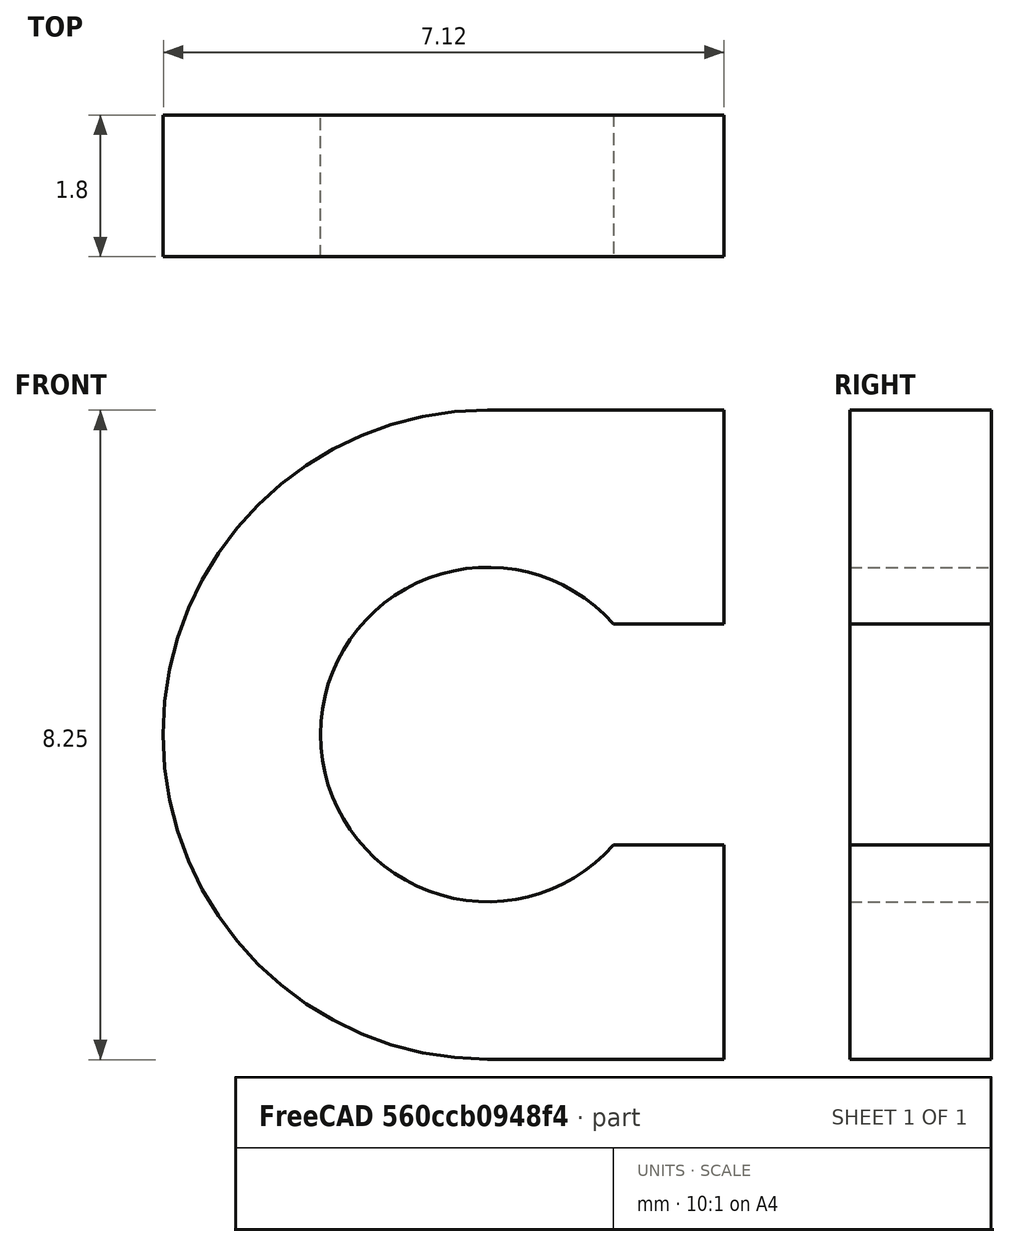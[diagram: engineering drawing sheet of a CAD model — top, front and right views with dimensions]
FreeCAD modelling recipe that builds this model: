
FCSTD DOCUMENT  (FreeCAD 0.21R33668 +26 (Git))
Label: Cover_shaft6
License: All rights reserved
LicenseURL: https://en.wikipedia.org/wiki/All_rights_reserved
objects: Sketcher::SketchObject×1, PartDesign::Pad×1, PartDesign::Body×1
note: 4 computed .brp shape members not serialized (recipe doc carries the construction recipe); baked Part::Feature solids carry a one-line shape summary decoded from their .brp

FEATURE [Sketcher::SketchObject] Sketch
  FullyConstrained = true
  MapMode = 5
  Placement = pos=(0,0,0) rot=(1,0,0;1.5708rad)
  Support = -> [XZ_Plane]
  sketch-geometry (8):
    g0: ArcOfCircle CenterX=0 CenterY=0 CenterZ=0 NormalX=0 NormalY=0 NormalZ=1 AngleXU=0 Radius=2.125 StartAngle=0.722386 EndAngle=5.5608
    g1: ArcOfCircle CenterX=0 CenterY=0 CenterZ=0 NormalX=0 NormalY=0 NormalZ=1 AngleXU=0 Radius=4.125 StartAngle=1.5708 EndAngle=4.71239
    g2: LineSegment StartX=-7e-16 StartY=4.125 StartZ=0 EndX=3 EndY=4.125 EndZ=0
    g3: LineSegment StartX=3 StartY=4.125 StartZ=0 EndX=3 EndY=1.405 EndZ=0
    g4: LineSegment StartX=3 StartY=-4.125 StartZ=0 EndX=-9e-16 EndY=-4.125 EndZ=0
    g5: LineSegment StartX=1.59424 StartY=1.405 StartZ=0 EndX=3 EndY=1.405 EndZ=0
    g6: LineSegment StartX=3 StartY=-1.405 StartZ=0 EndX=1.59424 EndY=-1.405 EndZ=0
    g7: LineSegment StartX=3 StartY=-1.405 StartZ=0 EndX=3 EndY=-4.125 EndZ=0
  constraints (22):
    c: Coincident(g0,g-1)
    c: Diameter(g0) = 4.25
    c: Coincident(g1,g0)
    c: Diameter(g1) = 8.25
    c: Coincident(g2,g3)
    c: Coincident(g7,g4)
    c: Horizontal(g2)
    c: Horizontal(g4)
    c: Vertical(g3)
    c: DistanceX(g0,g2) = 3
    c: Horizontal(g5)
    c: Horizontal(g6)
    c: Coincident(g0,g5)
    c: Coincident(g6,g0)
    c: Tangent(g1,g2) = 1.5708
    c: Tangent(g1,g4) = 1.5708
    c: Coincident(g3,g5)
    c: Coincident(g7,g6)
    c: Vertical(g6,g3)
    c: Vertical(g7)
    c: DistanceY(g3,g3) = 2.72
    c: DistanceY(g7,g7) = 2.72
FEATURE [PartDesign::Pad] Pad
  Direction = (0,-1,-2e-16)
  Length = 1.8
  Length2 = 10
  Placement = pos=(0,0,0) rot=(1,0,0;1.5708rad)
  Profile = -> Sketch
  ReferenceAxis = -> Sketch [N_Axis]
  Type = 0
FEATURE [PartDesign::Body] Body
  Group = -> [Sketch,Pad]
  Origin = -> Origin
  Tip = -> Pad
